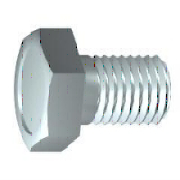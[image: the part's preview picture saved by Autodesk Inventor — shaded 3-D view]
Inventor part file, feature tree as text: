
AUTODESK INVENTOR PART (.ipt)
format: ipt  version: 2023.2 (Build 272271030, 271C)  size: 195,072 bytes
history: native  units: mm
features: sketch x2, revolve x1, thread x1, chamfer x1
ambient origin geometry x8: Origin, YZ Plane, XZ Plane, XY Plane, X Axis, Y Axis, Z Axis, Center Point
bodies: Solid1 (feature_tree)
feature tree (5):
  revolve  "Revolution1"  [1 undecoded]
  thread  "Thread1"  [1 undecoded]
  chamfer  "Chamfer1"  Distance=0.6mm
  sketch  "Sketch1"  dims[d0=25.5mm d1=10.0mm d3=20.0mm]
  sketch  "Sketch2"  dims[d4=15.5mm d5=0.6mm d6=90.0deg d14=18.0mm d15=0.0mm d16=0.833333mm d17=2.0mm d18=45.0deg d23=0.0mm d24=0.0mm d25=0.0mm d26=16.15mm d27=30.0deg d28=13.6mm d29=1.28mm d30=0.3mm d31=6.4mm d32=17.0mm d33=5.8mm d34=0.0mm]
note: 2 required parameter values undecoded (feature->parameter linkage not recoverable at this tier; creation-order binding heuristic only, values carry confidence <= 0.55)